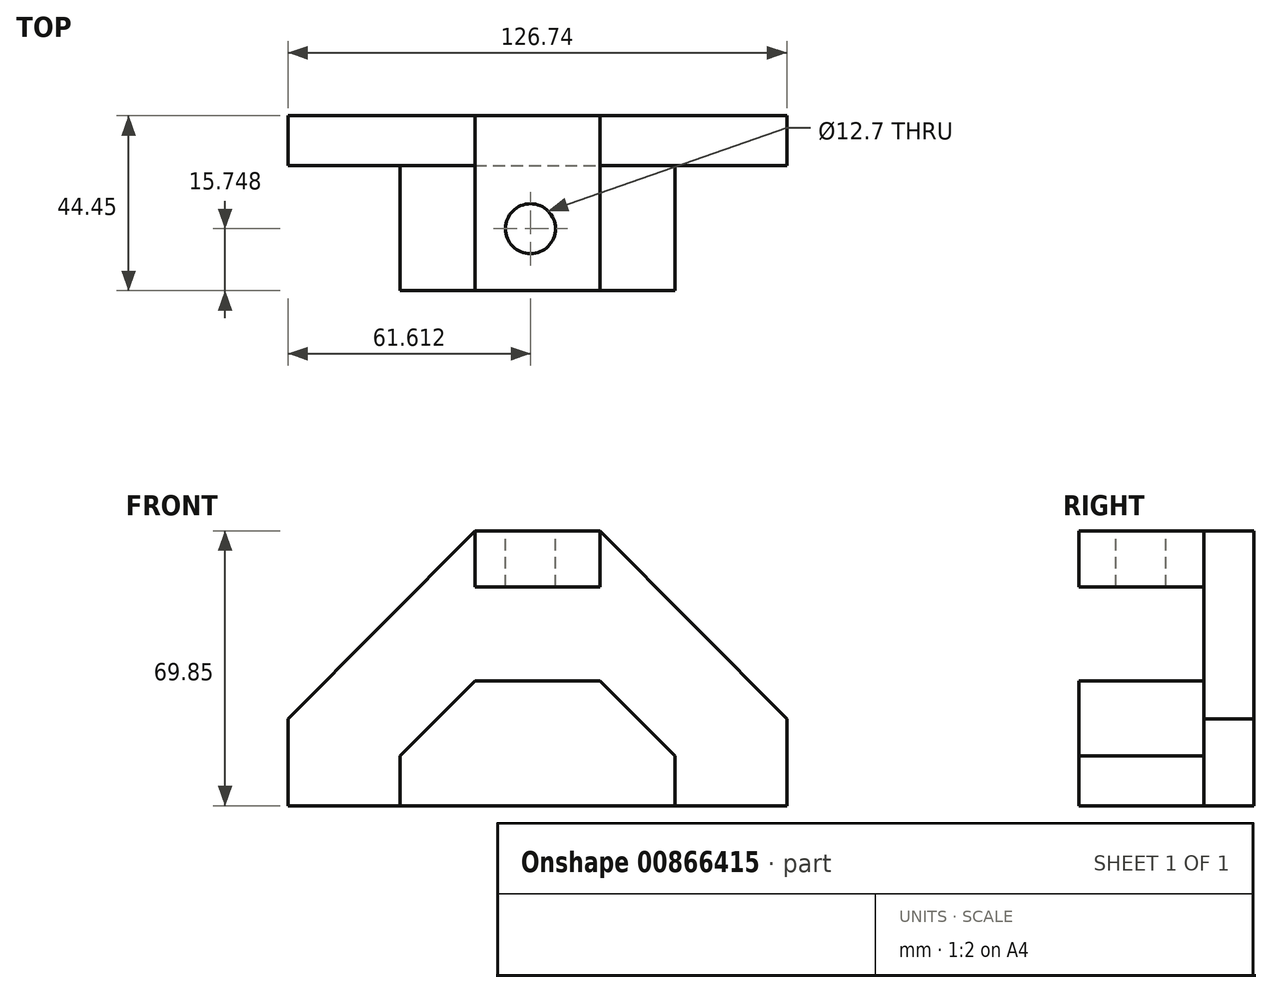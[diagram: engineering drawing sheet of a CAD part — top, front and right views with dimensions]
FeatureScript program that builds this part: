
annotation { "Feature Type Name" : "Feature", "Feature Type Description" : "" }
export const myFeature = defineFeature(function(context is Context, id is Id, definition is map)
    precondition{}
    {
        {
            var Q0;
            Q0=qCreatedBy(makeId("Front.planeOp"),FACE);
            var sketch = newSketch(context, id + "F0", { "sketchPlane" : qUnion([Q0])});
            skLineSegment(sketch, "E0", {"start": v(-6.95, 59.2) * mm, "end": v(24.8, 59.2) * mm});
            skLineSegment(sketch, "E1", {"start": v(24.8, 59.2) * mm, "end": v(72.3, 11.45) * mm});
            skLineSegment(sketch, "E2", {"start": v(72.3, 11.45) * mm, "end": v(72.3, -10.65) * mm});
            skLineSegment(sketch, "E3", {"start": v(72.3, -10.65) * mm, "end": v(-54.45, -10.65) * mm});
            skLineSegment(sketch, "E4", {"start": v(-6.95, 59.2) * mm, "end": v(-54.45, 11.45) * mm});
            skLineSegment(sketch, "E5", {"start": v(-54.45, 11.45) * mm, "end": v(-54.45, -10.65) * mm});
            skPoint(sketch, "E6.end.orphan", {"position": v(-66.14, 11.45) * mm});
            skSolve(sketch);
        }
        {
            var Q0;
            Q0 = qSketchRegion(id + "F0", true);
            extrude(context, id + "F1", {"entities" : qUnion([Q0]), "depth" : 12.7 * mm, "offsetDistance" : 25.4 * mm});
        }
        {
            var Q0;
            Q0=makeQuery(id+"F1.opExtrude","CAP_FACE",FACE,{"disambiguationData":[OSD([sQuery(id+"F0.wireOp",EDGE,"E0"),sQuery(id+"F0.wireOp",EDGE,"E1"),sQuery(id+"F0.wireOp",EDGE,"E2"),sQuery(id+"F0.wireOp",EDGE,"E3"),sQuery(id+"F0.wireOp",EDGE,"E4"),sQuery(id+"F0.wireOp",EDGE,"E5")])],"isStart":false});
            var sketch = newSketch(context, id + "F2", { "sketchPlane" : qUnion([Q0])});
            skLineSegment(sketch, "E7", {"start": v(-6.95, 59.2) * mm, "end": v(-6.95, 44.97) * mm});
            skLineSegment(sketch, "E8", {"start": v(-6.95, 44.97) * mm, "end": v(24.8, 44.97) * mm});
            skLineSegment(sketch, "E9", {"start": v(24.8, 44.97) * mm, "end": v(24.8, 59.2) * mm});
            skLineSegment(sketch, "E10", {"start": v(-6.95, 21.1) * mm, "end": v(24.8, 21.1) * mm});
            skLineSegment(sketch, "E11", {"start": v(24.8, 21.1) * mm, "end": v(43.85, 2.05) * mm});
            skLineSegment(sketch, "E12", {"start": v(43.85, 2.05) * mm, "end": v(43.85, -10.65) * mm});
            skLineSegment(sketch, "E13", {"start": v(-6.95, 21.1) * mm, "end": v(-26, 2.05) * mm});
            skLineSegment(sketch, "E14", {"start": v(-26, 2.05) * mm, "end": v(-26, -10.65) * mm});
            skSolve(sketch);
        }
        {
            var Q0;
            Q0=makeQuery(id+"F2.imprint","IMPRINT",FACE,{"disambiguationData":[TD([[makeQuery(id+"F2.imprint","IMPRINT",EDGE,{"derivedFrom":sQuery(id+"F2.wireOp",EDGE,"E7")}),1.0]])]});
            var Q1;
            Q1=makeQuery(id+"F2.imprint","IMPRINT",FACE,{"disambiguationData":[TD([[makeQuery(id+"F2.imprint","IMPRINT",EDGE,{"derivedFrom":sQuery(id+"F2.wireOp",EDGE,"E10")}),-1.0]])]});
            extrude(context, id + "F3", {"entities" : qUnion([Q0, Q1]), "operationType" : NewBodyOperationType.ADD, "depth" : 31.75 * mm, "offsetDistance" : 25.4 * mm});
        }
        {
            var Q0;
            {var subQ0=sQuery(id+"F0.wireOp",EDGE,"E0");Q0=makeQuery(id+"F3.boolean.opBoolean","MERGE",FACE,{"derivedFrom":[makeQuery(id+"F1.opExtrude","SWEPT_FACE",FACE,{"disambiguationData":[OSD([subQ0])]}),makeQuery(id+"F3.opExtrude","SWEPT_FACE",FACE,{"disambiguationData":[OSD([subQ0])]})]});}
            var sketch = newSketch(context, id + "F4", { "sketchPlane" : qUnion([Q0])});
            skCircle(sketch, "E15", {"center": v(7.16, -28.7) * mm, "radius": 6.35 * mm});
            skSolve(sketch);
        }
        {
            var Q0;
            Q0 = qSketchRegion(id + "F4", true);
            extrude(context, id + "F5", {"entities" : qUnion([Q0]), "operationType" : NewBodyOperationType.REMOVE, "oppositeDirection" : true, "depth" : 25.4 * mm, "offsetDistance" : 25.4 * mm});
        }
    });
